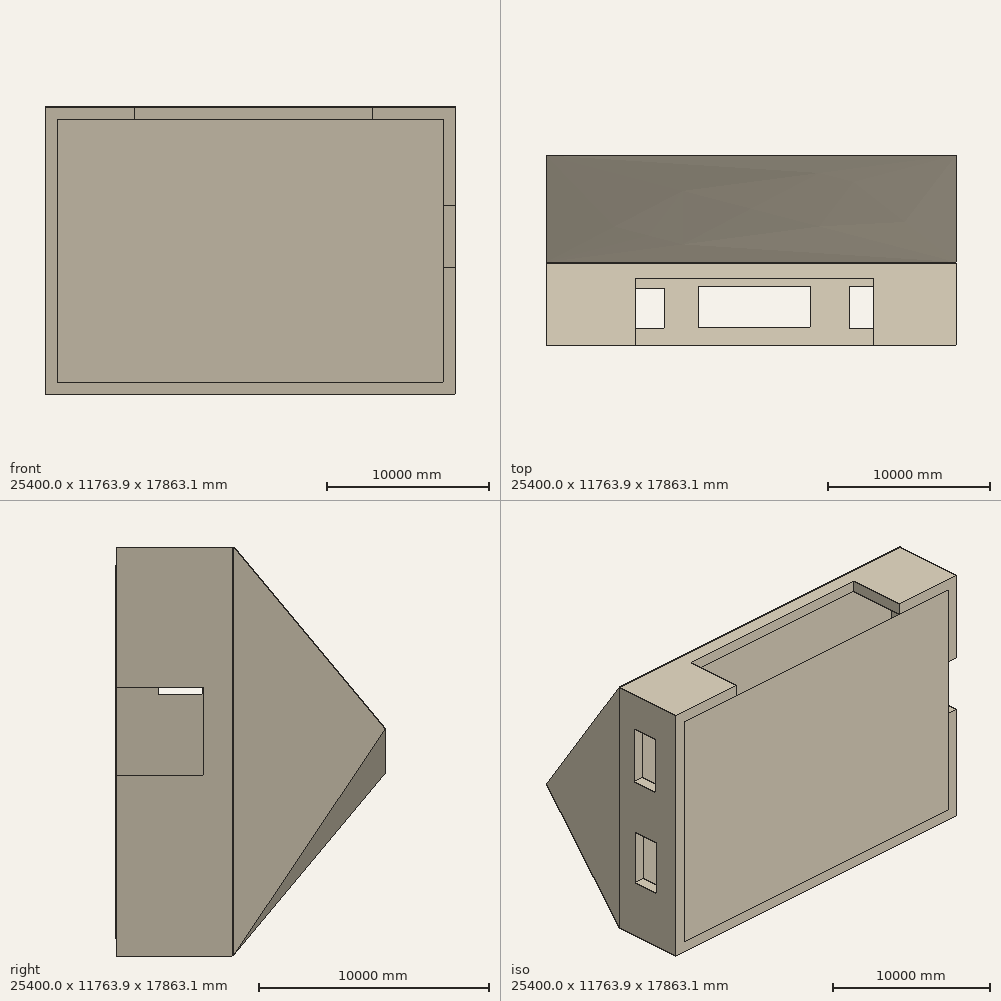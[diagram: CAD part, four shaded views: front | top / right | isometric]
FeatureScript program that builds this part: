
annotation { "Feature Type Name" : "Feature", "Feature Type Description" : "" }
export const myFeature = defineFeature(function(context is Context, id is Id, definition is map)
    precondition{}
    {
        {
            var Q0;
            Q0=qCreatedBy(makeId("Front.planeOp"),FACE);
            var sketch = newSketch(context, id + "F0", { "sketchPlane" : qUnion([Q0])});
            skLineSegment(sketch, "E0.bottom", {"start": v(-12698.24, 8529.1) * mm, "end": v(12701.76, 8529.1) * mm});
            skLineSegment(sketch, "E0.top", {"start": v(-12698.24, -9250.9) * mm, "end": v(12701.76, -9250.9) * mm});
            skLineSegment(sketch, "E0.left", {"start": v(-12698.24, 8529.1) * mm, "end": v(-12698.24, -9250.9) * mm});
            skLineSegment(sketch, "E0.right", {"start": v(12701.76, 8529.1) * mm, "end": v(12701.76, -9250.9) * mm});
            skLineSegment(sketch, "E1.bottom", {"start": v(11939.76, 7767.1) * mm, "end": v(-11936.24, 7767.1) * mm});
            skLineSegment(sketch, "E1.top", {"start": v(11939.76, -8488.9) * mm, "end": v(-11936.24, -8488.9) * mm});
            skLineSegment(sketch, "E1.left", {"start": v(11939.76, 7767.1) * mm, "end": v(11939.76, -8488.9) * mm});
            skLineSegment(sketch, "E1.right", {"start": v(-11936.24, 7767.1) * mm, "end": v(-11936.24, -8488.9) * mm});
            skLineSegment(sketch, "E2.bottom", {"start": v(7546.78, 8529.1) * mm, "end": v(-7201.79, 8529.1) * mm});
            skLineSegment(sketch, "E2.top", {"start": v(7546.78, 7767.1) * mm, "end": v(-7201.79, 7767.1) * mm});
            skLineSegment(sketch, "E2.left", {"start": v(7546.78, 8529.1) * mm, "end": v(7546.78, 7767.1) * mm});
            skLineSegment(sketch, "E2.right", {"start": v(-7201.79, 8529.1) * mm, "end": v(-7201.79, 7767.1) * mm});
            skLineSegment(sketch, "E3.bottom", {"start": v(-11936.24, 6250.27) * mm, "end": v(-12698.24, 6250.27) * mm});
            skLineSegment(sketch, "E3.top", {"start": v(-11936.24, 2440.27) * mm, "end": v(-12698.24, 2440.27) * mm});
            skLineSegment(sketch, "E3.left", {"start": v(-11936.24, 6250.27) * mm, "end": v(-11936.24, 2440.27) * mm});
            skLineSegment(sketch, "E3.right", {"start": v(-12698.24, 6250.27) * mm, "end": v(-12698.24, 2440.27) * mm});
            skLineSegment(sketch, "E4.bottom", {"start": v(11939.76, 2440.27) * mm, "end": v(12701.76, 2440.27) * mm});
            skLineSegment(sketch, "E4.top", {"start": v(11939.76, -1369.73) * mm, "end": v(12701.76, -1369.73) * mm});
            skLineSegment(sketch, "E4.left", {"start": v(11939.76, 2440.27) * mm, "end": v(11939.76, -1369.73) * mm});
            skLineSegment(sketch, "E4.right", {"start": v(12701.76, 2440.27) * mm, "end": v(12701.76, -1369.73) * mm});
            skLineSegment(sketch, "E5.bottom", {"start": v(8530.7, -8488.9) * mm, "end": v(4720.7, -8488.9) * mm});
            skLineSegment(sketch, "E5.top", {"start": v(8530.7, -9250.9) * mm, "end": v(4720.7, -9250.9) * mm});
            skLineSegment(sketch, "E5.left", {"start": v(8530.7, -8488.9) * mm, "end": v(8530.7, -9250.9) * mm});
            skLineSegment(sketch, "E5.right", {"start": v(4720.7, -8488.9) * mm, "end": v(4720.7, -9250.9) * mm});
            skLineSegment(sketch, "E6.bottom", {"start": v(923.17, -8488.9) * mm, "end": v(-3227.63, -8488.9) * mm});
            skLineSegment(sketch, "E6.top", {"start": v(923.17, -9250.9) * mm, "end": v(-3227.63, -9250.9) * mm});
            skLineSegment(sketch, "E6.left", {"start": v(923.17, -8488.9) * mm, "end": v(923.17, -9250.9) * mm});
            skLineSegment(sketch, "E6.right", {"start": v(-3227.63, -8488.9) * mm, "end": v(-3227.63, -9250.9) * mm});
            skLineSegment(sketch, "E7.bottom", {"start": v(-5511.34, -8488.9) * mm, "end": v(-9321.34, -8488.9) * mm});
            skLineSegment(sketch, "E7.top", {"start": v(-5511.34, -9250.9) * mm, "end": v(-9321.34, -9250.9) * mm});
            skLineSegment(sketch, "E7.left", {"start": v(-5511.34, -8488.9) * mm, "end": v(-5511.34, -9250.9) * mm});
            skLineSegment(sketch, "E7.right", {"start": v(-9321.34, -8488.9) * mm, "end": v(-9321.34, -9250.9) * mm});
            skLineSegment(sketch, "E8.bottom", {"start": v(-11936.24, -1369.73) * mm, "end": v(-12698.24, -1369.73) * mm});
            skLineSegment(sketch, "E8.top", {"start": v(-11936.24, -5179.73) * mm, "end": v(-12698.24, -5179.73) * mm});
            skLineSegment(sketch, "E8.left", {"start": v(-11936.24, -1369.73) * mm, "end": v(-11936.24, -5179.73) * mm});
            skLineSegment(sketch, "E8.right", {"start": v(-12698.24, -1369.73) * mm, "end": v(-12698.24, -5179.73) * mm});
            skSolve(sketch);
        }
        {
            var Q0;
            {var subQ4=sQuery(id+"F0.wireOp",EDGE,"E2.left");Q0=makeQuery(id+"F0.imprint","IMPRINT",FACE,{"disambiguationData":[TD([[makeQuery(id+"F0.imprint","IMPRINT",EDGE,{"derivedFrom":subQ4}),1.0]])]});}
            var Q1;
            {var subQ7=sQuery(id+"F0.wireOp",EDGE,"E4.top");Q1=makeQuery(id+"F0.imprint","IMPRINT",FACE,{"disambiguationData":[TD([[makeQuery(id+"F0.imprint","IMPRINT",EDGE,{"derivedFrom":subQ7}),-1.0]])]});}
            var Q2;
            {var subQ0=sQuery(id+"F0.wireOp",EDGE,"E5.right");Q2=makeQuery(id+"F0.imprint","IMPRINT",FACE,{"disambiguationData":[TD([[makeQuery(id+"F0.imprint","IMPRINT",EDGE,{"derivedFrom":subQ0}),-1.0]])]});}
            var Q3;
            {var subQ2=sQuery(id+"F0.wireOp",EDGE,"E6.left");Q3=makeQuery(id+"F0.imprint","IMPRINT",FACE,{"disambiguationData":[TD([[makeQuery(id+"F0.imprint","IMPRINT",EDGE,{"derivedFrom":subQ2}),-1.0]])]});}
            var Q4;
            {var subQ0=sQuery(id+"F0.wireOp",EDGE,"E6.right");Q4=makeQuery(id+"F0.imprint","IMPRINT",FACE,{"disambiguationData":[TD([[makeQuery(id+"F0.imprint","IMPRINT",EDGE,{"derivedFrom":subQ0}),-1.0]])]});}
            var Q5;
            {var subQ4=sQuery(id+"F0.wireOp",EDGE,"E7.right");Q5=makeQuery(id+"F0.imprint","IMPRINT",FACE,{"disambiguationData":[TD([[makeQuery(id+"F0.imprint","IMPRINT",EDGE,{"derivedFrom":subQ4}),-1.0]])]});}
            var Q6;
            {var subQ0=sQuery(id+"F0.wireOp",EDGE,"E3.top");Q6=makeQuery(id+"F0.imprint","IMPRINT",FACE,{"disambiguationData":[TD([[makeQuery(id+"F0.imprint","IMPRINT",EDGE,{"derivedFrom":subQ0}),1.0]])]});}
            var Q7;
            {var subQ4=sQuery(id+"F0.wireOp",EDGE,"E2.right");Q7=makeQuery(id+"F0.imprint","IMPRINT",FACE,{"disambiguationData":[TD([[makeQuery(id+"F0.imprint","IMPRINT",EDGE,{"derivedFrom":subQ4}),-1.0]])]});}
            var Q8;
            {var subQ0=sQuery(id+"F0.wireOp",EDGE,"E3.bottom");Q8=makeQuery(id+"F0.imprint","IMPRINT",FACE,{"disambiguationData":[TD([[makeQuery(id+"F0.imprint","IMPRINT",EDGE,{"derivedFrom":subQ0}),1.0]])]});}
            var Q9;
            {var subQ2=sQuery(id+"F0.wireOp",EDGE,"E8.bottom");Q9=makeQuery(id+"F0.imprint","IMPRINT",FACE,{"disambiguationData":[TD([[makeQuery(id+"F0.imprint","IMPRINT",EDGE,{"derivedFrom":subQ2}),1.0]])]});}
            var Q10;
            {var subQ0=sQuery(id+"F0.wireOp",EDGE,"E7.left");Q10=makeQuery(id+"F0.imprint","IMPRINT",FACE,{"disambiguationData":[TD([[makeQuery(id+"F0.imprint","IMPRINT",EDGE,{"derivedFrom":subQ0}),-1.0]])]});}
            var Q11;
            {var subQ2=sQuery(id+"F0.wireOp",EDGE,"E2.left");Q11=makeQuery(id+"F0.imprint","IMPRINT",FACE,{"disambiguationData":[TD([[makeQuery(id+"F0.imprint","IMPRINT",EDGE,{"derivedFrom":subQ2}),-1.0]])]});}
            var Q12;
            {var subQ0=sQuery(id+"F0.wireOp",EDGE,"E5.left");Q12=makeQuery(id+"F0.imprint","IMPRINT",FACE,{"disambiguationData":[TD([[makeQuery(id+"F0.imprint","IMPRINT",EDGE,{"derivedFrom":subQ0}),-1.0]])]});}
            var Q13;
            {var subQ2=sQuery(id+"F0.wireOp",EDGE,"E4.bottom");Q13=makeQuery(id+"F0.imprint","IMPRINT",FACE,{"disambiguationData":[TD([[makeQuery(id+"F0.imprint","IMPRINT",EDGE,{"derivedFrom":subQ2}),-1.0]])]});}
            extrude(context, id + "F1", {"entities" : qUnion([Q0, Q1, Q2, Q3, Q4, Q5, Q6, Q7, Q8, Q9, Q10, Q11, Q12, Q13]), "surfaceOperationType" : NewSurfaceOperationType.ADD, "oppositeDirection" : true, "depth" : 5080 * mm, "offsetDistance" : 25.4 * mm});
        }
        {
            var Q0;
            Q0=makeQuery(id+"F1.opExtrude","SWEPT_FACE",FACE,{"disambiguationData":[OSD([sQuery(id+"F0.wireOp",EDGE,"E0.right")])]});
            var sketch = newSketch(context, id + "F2", { "sketchPlane" : qUnion([Q0])});
            skLineSegment(sketch, "E9.bottom", {"start": v(0, 2440.27) * mm, "end": v(3810, 2440.27) * mm});
            skLineSegment(sketch, "E9.top", {"start": v(0, -1369.73) * mm, "end": v(3810, -1369.73) * mm});
            skLineSegment(sketch, "E9.left", {"start": v(0, 2440.27) * mm, "end": v(0, -1369.73) * mm});
            skLineSegment(sketch, "E9.right", {"start": v(3810, 2440.27) * mm, "end": v(3810, -1369.73) * mm});
            skSolve(sketch);
        }
        {
            var Q0;
            Q0=makeQuery(id+"F1.opExtrude","SWEPT_FACE",FACE,{"disambiguationData":[OSD([sQuery(id+"F0.wireOp",EDGE,"E0.bottom")])]});
            var sketch = newSketch(context, id + "F3", { "sketchPlane" : qUnion([Q0])});
            skLineSegment(sketch, "E10.bottom", {"start": v(-7201.79, 0) * mm, "end": v(7546.78, 0) * mm});
            skLineSegment(sketch, "E10.top", {"start": v(-7201.79, 4147.14) * mm, "end": v(7546.78, 4147.14) * mm});
            skLineSegment(sketch, "E10.left", {"start": v(-7201.79, 0) * mm, "end": v(-7201.79, 4147.14) * mm});
            skLineSegment(sketch, "E10.right", {"start": v(7546.78, 0) * mm, "end": v(7546.78, 4147.14) * mm});
            skSolve(sketch);
        }
        {
            var Q0;
            Q0=makeQuery(id+"F1.opExtrude","SWEPT_FACE",FACE,{"disambiguationData":[OSD([sQuery(id+"F0.wireOp",EDGE,"E0.left")])]});
            var sketch = newSketch(context, id + "F4", { "sketchPlane" : qUnion([Q0])});
            skLineSegment(sketch, "E11.bottom", {"start": v(-3696.68, -5313.06) * mm, "end": v(-1793.16, -5313.06) * mm});
            skLineSegment(sketch, "E11.top", {"start": v(-3696.68, -1578.35) * mm, "end": v(-1793.16, -1578.35) * mm});
            skLineSegment(sketch, "E11.left", {"start": v(-3696.68, -5313.06) * mm, "end": v(-3696.68, -1578.35) * mm});
            skLineSegment(sketch, "E11.right", {"start": v(-1793.16, -5313.06) * mm, "end": v(-1793.16, -1578.35) * mm});
            skLineSegment(sketch, "E12.bottom", {"start": v(-3783.76, 2127.63) * mm, "end": v(-1852.4, 2127.63) * mm});
            skLineSegment(sketch, "E12.top", {"start": v(-3783.76, 6033.61) * mm, "end": v(-1852.4, 6033.61) * mm});
            skLineSegment(sketch, "E12.left", {"start": v(-3783.76, 2127.63) * mm, "end": v(-3783.76, 6033.61) * mm});
            skLineSegment(sketch, "E12.right", {"start": v(-1852.4, 2127.63) * mm, "end": v(-1852.4, 6033.61) * mm});
            skSolve(sketch);
        }
        {
            var Q0;
            Q0=makeQuery(id+"F1.opExtrude","SWEPT_FACE",FACE,{"disambiguationData":[OSD([sQuery(id+"F0.wireOp",EDGE,"E0.top")])]});
            var sketch = newSketch(context, id + "F5", { "sketchPlane" : qUnion([Q0])});
            skLineSegment(sketch, "E13.bottom", {"start": v(-11194.34, -1048.84) * mm, "end": v(-5394.33, -1048.84) * mm});
            skLineSegment(sketch, "E13.top", {"start": v(-11194.34, -3512.68) * mm, "end": v(-5394.33, -3512.68) * mm});
            skLineSegment(sketch, "E13.left", {"start": v(-11194.34, -1048.84) * mm, "end": v(-11194.34, -3512.68) * mm});
            skLineSegment(sketch, "E13.right", {"start": v(-5394.33, -1048.84) * mm, "end": v(-5394.33, -3512.68) * mm});
            skLineSegment(sketch, "E14.bottom", {"start": v(-3253.86, -1085.63) * mm, "end": v(3633.38, -1085.63) * mm});
            skLineSegment(sketch, "E14.top", {"start": v(-3253.86, -3626.68) * mm, "end": v(3633.38, -3626.68) * mm});
            skLineSegment(sketch, "E14.left", {"start": v(-3253.86, -1085.63) * mm, "end": v(-3253.86, -3626.68) * mm});
            skLineSegment(sketch, "E14.right", {"start": v(3633.38, -1085.63) * mm, "end": v(3633.38, -3626.68) * mm});
            skLineSegment(sketch, "E15.bottom", {"start": v(6043.36, -1048.84) * mm, "end": v(11176.16, -1048.84) * mm});
            skLineSegment(sketch, "E15.top", {"start": v(6043.36, -3605.49) * mm, "end": v(11176.16, -3605.49) * mm});
            skLineSegment(sketch, "E15.left", {"start": v(6043.36, -1048.84) * mm, "end": v(6043.36, -3605.49) * mm});
            skLineSegment(sketch, "E15.right", {"start": v(11176.16, -1048.84) * mm, "end": v(11176.16, -3605.49) * mm});
            skSolve(sketch);
        }
        {
            var Q0;
            Q0 = qSketchRegion(id + "F2", true);
            extrude(context, id + "F6", {"entities" : qUnion([Q0]), "operationType" : NewBodyOperationType.REMOVE, "endBound" : BoundingType.UP_TO_NEXT, "oppositeDirection" : true, "depth" : 25.4 * mm, "offsetDistance" : 25.4 * mm});
        }
        {
            var Q0;
            Q0=makeQuery(id+"F3.imprint","IMPRINT",FACE,{"disambiguationData":[TD([[makeQuery(id+"F3.imprint","IMPRINT",EDGE,{"derivedFrom":sQuery(id+"F3.wireOp",EDGE,"E10.bottom")}),1.0]])]});
            extrude(context, id + "F7", {"entities" : qUnion([Q0]), "operationType" : NewBodyOperationType.REMOVE, "endBound" : BoundingType.UP_TO_NEXT, "oppositeDirection" : true, "depth" : 25.4 * mm, "offsetDistance" : 25.4 * mm});
        }
        {
            var Q0;
            {var subQ11=sQuery(id+"F0.wireOp",EDGE,"E1.bottom");var subQ12=makeQuery(id+"F0.imprint","INTERSECT",VERTEX,{"derivedFrom":[subQ11,sQuery(id+"F0.wireOp",EDGE,"E2.left")]});Q0=makeQuery(id+"F0.imprint","IMPRINT",FACE,{"disambiguationData":[TD([[makeQuery(id+"F0.imprint","IMPRINT",EDGE,{"disambiguationData":[TD([[subQ12,-1.0]])],"derivedFrom":subQ11}),1.0]])]});}
            extrude(context, id + "F8", {"entities" : qUnion([Q0]), "depth" : 25.4 * mm, "offsetDistance" : 25.4 * mm});
        }
        {
            var Q0;
            Q0=makeQuery(id+"F5.imprint","IMPRINT",FACE,{"disambiguationData":[TD([[makeQuery(id+"F5.imprint","IMPRINT",EDGE,{"derivedFrom":sQuery(id+"F5.wireOp",EDGE,"E15.bottom")}),-1.0]])]});
            var Q1;
            Q1=makeQuery(id+"F5.imprint","IMPRINT",FACE,{"disambiguationData":[TD([[makeQuery(id+"F5.imprint","IMPRINT",EDGE,{"derivedFrom":sQuery(id+"F5.wireOp",EDGE,"E13.bottom")}),-1.0]])]});
            var Q2;
            Q2=makeQuery(id+"F5.imprint","IMPRINT",FACE,{"disambiguationData":[TD([[makeQuery(id+"F5.imprint","IMPRINT",EDGE,{"derivedFrom":sQuery(id+"F5.wireOp",EDGE,"E14.bottom")}),-1.0]])]});
            extrude(context, id + "F9", {"entities" : qUnion([Q0, Q1, Q2]), "operationType" : NewBodyOperationType.REMOVE, "endBound" : BoundingType.UP_TO_NEXT, "oppositeDirection" : true, "depth" : 25.4 * mm, "offsetDistance" : 25.4 * mm});
        }
        {
            var Q0;
            Q0=makeQuery(id+"F4.imprint","IMPRINT",FACE,{"disambiguationData":[TD([[makeQuery(id+"F4.imprint","IMPRINT",EDGE,{"derivedFrom":sQuery(id+"F4.wireOp",EDGE,"E11.bottom")}),-1.0]])]});
            var sketch = newSketch(context, id + "F10", { "sketchPlane" : qUnion([Q0])});
            skLineSegment(sketch, "E16", {"start": v(-5095.45, 8573.72) * mm, "end": v(-11722.15, -1320.63) * mm});
            skLineSegment(sketch, "E17", {"start": v(-11722.15, -1320.63) * mm, "end": v(-5095.45, -9272.66) * mm});
            skLineSegment(sketch, "E18", {"start": v(-5095.45, 8573.72) * mm, "end": v(-5095.45, -9272.66) * mm});
            skSolve(sketch);
        }
        {
            var Q0;
            Q0=makeQuery(id+"F4.imprint","IMPRINT",FACE,{"disambiguationData":[TD([[makeQuery(id+"F4.imprint","IMPRINT",EDGE,{"derivedFrom":sQuery(id+"F4.wireOp",EDGE,"E12.bottom")}),1.0]])]});
            var Q1;
            Q1=makeQuery(id+"F4.imprint","IMPRINT",FACE,{"disambiguationData":[TD([[makeQuery(id+"F4.imprint","IMPRINT",EDGE,{"derivedFrom":sQuery(id+"F4.wireOp",EDGE,"E11.bottom")}),1.0]])]});
            extrude(context, id + "F11", {"entities" : qUnion([Q0, Q1]), "operationType" : NewBodyOperationType.REMOVE, "endBound" : BoundingType.UP_TO_NEXT, "oppositeDirection" : true, "depth" : 25.4 * mm, "offsetDistance" : 25.4 * mm});
        }
        {
            var Q0;
            Q0=makeQuery(id+"F1.opExtrude","SWEPT_FACE",FACE,{"disambiguationData":[OSD([sQuery(id+"F0.wireOp",EDGE,"E0.right")])]});
            var sketch = newSketch(context, id + "F12", { "sketchPlane" : qUnion([Q0])});
            skLineSegment(sketch, "E19", {"start": v(5111.77, -9255.92) * mm, "end": v(11738.46, 638.42) * mm});
            skLineSegment(sketch, "E20", {"start": v(11738.46, 638.42) * mm, "end": v(5111.77, 8590.45) * mm});
            skLineSegment(sketch, "E21", {"start": v(5111.77, -9255.92) * mm, "end": v(5111.77, 8590.45) * mm});
            skSolve(sketch);
        }
        {
            var Q0;
            Q0=makeQuery(id+"F12.imprint","IMPRINT",FACE,{"disambiguationData":[TD([[makeQuery(id+"F12.imprint","IMPRINT",EDGE,{"derivedFrom":sQuery(id+"F12.wireOp",EDGE,"E19")}),1.0]])]});
            var Q1;
            Q1=makeQuery(id+"F10.imprint","IMPRINT",FACE,{"disambiguationData":[TD([[makeQuery(id+"F10.imprint","IMPRINT",EDGE,{"derivedFrom":sQuery(id+"F10.wireOp",EDGE,"E16")}),1.0]])]});
            loft(context, id + "F13", {"sheetProfilesArray" : [{ "sheetProfileEntities" : qUnion([Q0]) }, { "sheetProfileEntities" : qUnion([Q1]) }]});
        }
    });
